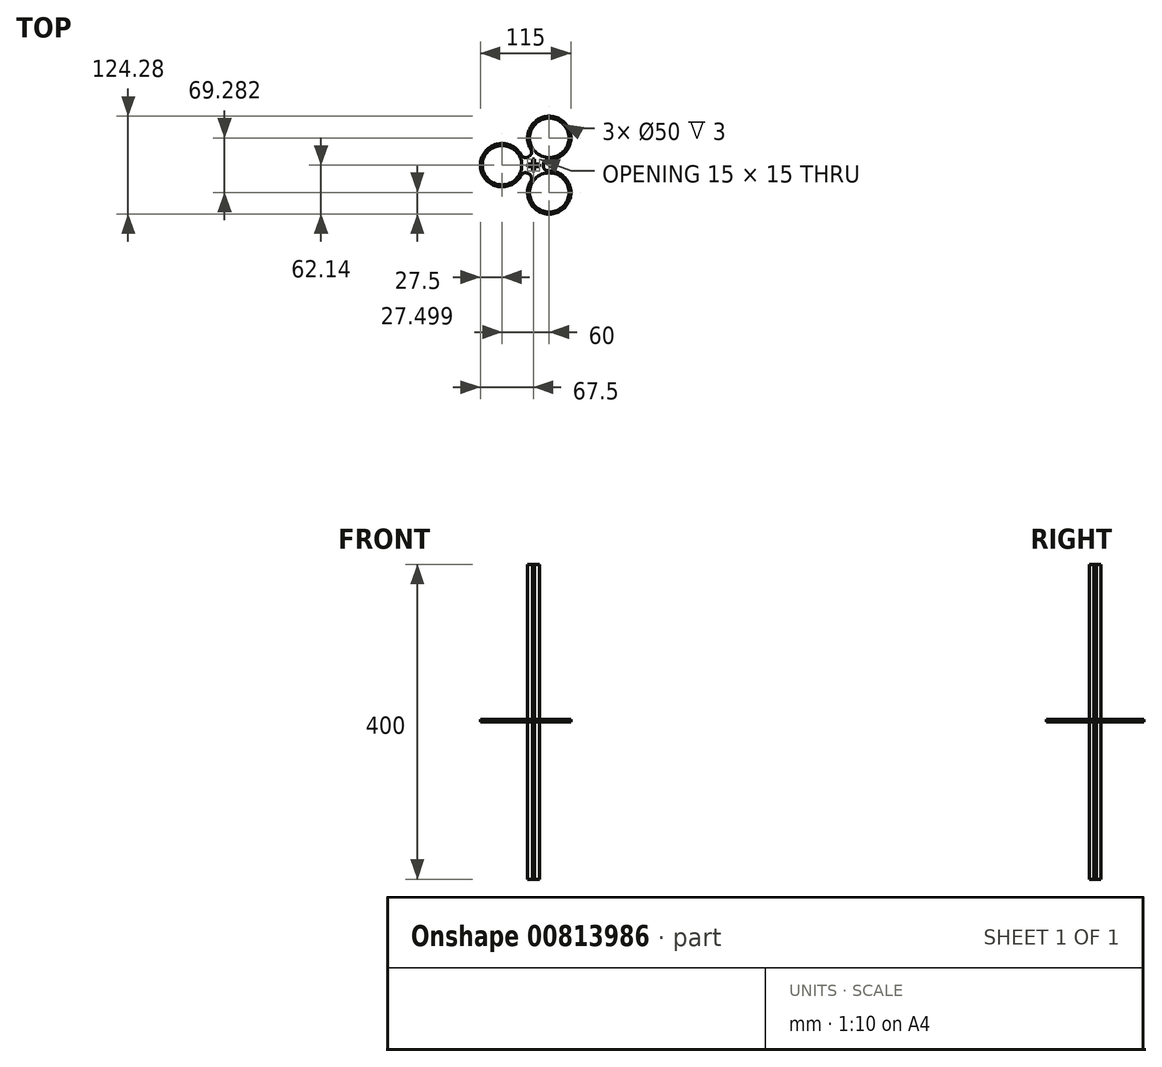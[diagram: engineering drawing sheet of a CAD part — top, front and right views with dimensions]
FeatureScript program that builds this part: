
annotation { "Feature Type Name" : "Feature", "Feature Type Description" : "" }
export const myFeature = defineFeature(function(context is Context, id is Id, definition is map)
    precondition{}
    {
        {
            assignVariable(context, id + "F0", {"variableType" : VariableType.LENGTH, "name" : "wt", "lengthValue" : 3 * mm});
        }
        {
            var Q0;
            Q0=qCreatedBy(makeId("Top.planeOp"),FACE);
            var sketch = newSketch(context, id + "F1", { "sketchPlane" : qUnion([Q0])});
            skCircle(sketch, "E0", {"center": v(0, 0) * mm, "radius": 12.5 * mm});
            skCircle(sketch, "E1", {"center": v(-40, 0) * mm, "radius": 27.5 * mm});
            skLineSegment(sketch, "E2", {"start": v(20, 34.64) * mm, "end": v(-40, 0) * mm, "construction": true});
            skPoint(sketch, "E3", {"position": v(-10, 17.32) * mm});
            skLineSegment(sketch, "E4", {"start": v(-10, 17.32) * mm, "end": v(0, 0) * mm, "construction": true});
            skLineSegment(sketch, "E5", {"start": v(20, 34.64) * mm, "end": v(20, -34.64) * mm, "construction": true});
            skLineSegment(sketch, "E6", {"start": v(-40, 0) * mm, "end": v(20, -34.64) * mm, "construction": true});
            skLineSegment(sketch, "E7", {"start": v(0, 0) * mm, "end": v(20, 0) * mm, "construction": true});
            skLineSegment(sketch, "E8", {"start": v(0, 0) * mm, "end": v(-10, -17.32) * mm, "construction": true});
            skLineSegment(sketch, "E9.bottom", {"start": v(-7.5, 1.5) * mm, "end": v(7.5, 1.5) * mm});
            skLineSegment(sketch, "E9.top", {"start": v(-7.5, -1.5) * mm, "end": v(7.5, -1.5) * mm});
            skLineSegment(sketch, "E9.left", {"start": v(-7.5, 1.5) * mm, "end": v(-7.5, -1.5) * mm});
            skLineSegment(sketch, "E9.right", {"start": v(7.5, 1.5) * mm, "end": v(7.5, -1.5) * mm});
            skLineSegment(sketch, "E10.bottom", {"start": v(-1.5, 7.5) * mm, "end": v(1.5, 7.5) * mm});
            skLineSegment(sketch, "E10.top", {"start": v(-1.5, -7.5) * mm, "end": v(1.5, -7.5) * mm});
            skLineSegment(sketch, "E10.left", {"start": v(-1.5, 7.5) * mm, "end": v(-1.5, -7.5) * mm});
            skLineSegment(sketch, "E10.right", {"start": v(1.5, 7.5) * mm, "end": v(1.5, -7.5) * mm});
            skCircle(sketch, "E11", {"center": v(-40, 0) * mm, "radius": 25 * mm});
            skCircle(sketch, "E12.1.0", {"center": v(20, -34.64) * mm, "radius": 27.5 * mm});
            skCircle(sketch, "E12.1.1", {"center": v(20, -34.64) * mm, "radius": 25 * mm});
            skCircle(sketch, "E12.2.0", {"center": v(20, 34.64) * mm, "radius": 27.5 * mm});
            skCircle(sketch, "E12.2.1", {"center": v(20, 34.64) * mm, "radius": 25 * mm});
            skFitSpline(sketch, "E13", {"points": [v(-16.18, 13.75) * mm, v(-6.25, 10.83) * mm, v(-3.82, 20.9) * mm], "startDerivative": vector(16.88, -30.59) * mm, "endDerivative": vector(-18.05, 29.91) * mm});
            skFitSpline(sketch, "E14", {"points": [v(20, 7.14) * mm, v(12.5, 0) * mm, v(20, -7.14) * mm], "startDerivative": vector(-34.93, 0.67) * mm, "endDerivative": vector(34.93, 0.67) * mm});
            skFitSpline(sketch, "E15", {"points": [v(-3.82, -20.9) * mm, v(-6.25, -10.83) * mm, v(-16.18, -13.75) * mm], "startDerivative": vector(18.05, 29.91) * mm, "endDerivative": vector(-16.88, -30.59) * mm});
            skLineSegment(sketch, "E16", {"start": v(20, 34.64) * mm, "end": v(14.18, 7.25) * mm, "construction": true});
            skLineSegment(sketch, "E17.MirrorCS", {"start": v(20, -34.64) * mm, "end": v(14.18, -7.25) * mm, "construction": true});
            skLineSegment(sketch, "E18", {"start": v(20, -34.64) * mm, "end": v(-0.8, -15.9) * mm, "construction": true});
            skLineSegment(sketch, "E19.MirrorCS", {"start": v(-40, 0) * mm, "end": v(-13.37, -8.65) * mm, "construction": true});
            skLineSegment(sketch, "E20.MirrorCS", {"start": v(-40, 0) * mm, "end": v(-13.37, 8.65) * mm, "construction": true});
            skLineSegment(sketch, "E21.MirrorCS", {"start": v(20, 34.64) * mm, "end": v(-0.8, 15.9) * mm, "construction": true});
            skSolve(sketch);
        }
        {
            var Q0;
            Q0=makeQuery(id+"F1.imprint","IMPRINT",FACE,{"disambiguationData":[TD([[makeQuery(id+"F1.imprint","IMPRINT",EDGE,{"derivedFrom":sQuery(id+"F1.wireOp",EDGE,"E11")}),-1.0]])]});
            var Q1;
            {var subQ0=sQuery(id+"F1.wireOp",EDGE,"E13");var subQ1=sQuery(id+"F1.wireOp",EDGE,"E0");var subQ2=makeQuery(id+"F1.imprint","INTERSECT",VERTEX,{"derivedFrom":[subQ1,subQ0]});Q1=makeQuery(id+"F1.imprint","IMPRINT",FACE,{"disambiguationData":[TD([[makeQuery(id+"F1.imprint","IMPRINT",EDGE,{"disambiguationData":[TD([[subQ2,-1.0]])],"derivedFrom":subQ1}),-1.0]])]});}
            var Q2;
            {var subQ0=sQuery(id+"F1.wireOp",EDGE,"E13");var subQ1=sQuery(id+"F1.wireOp",EDGE,"E0");var subQ2=makeQuery(id+"F1.imprint","INTERSECT",VERTEX,{"derivedFrom":[subQ1,subQ0]});Q2=makeQuery(id+"F1.imprint","IMPRINT",FACE,{"disambiguationData":[TD([[makeQuery(id+"F1.imprint","IMPRINT",EDGE,{"disambiguationData":[TD([[subQ2,1.0]])],"derivedFrom":subQ1}),-1.0]])]});}
            var Q3;
            Q3=makeQuery(id+"F1.imprint","IMPRINT",FACE,{"disambiguationData":[TD([[makeQuery(id+"F1.imprint","IMPRINT",EDGE,{"derivedFrom":sQuery(id+"F1.wireOp",EDGE,"E12.2.1")}),-1.0]])]});
            var Q4;
            {var subQ0=sQuery(id+"F1.wireOp",EDGE,"E14");var subQ1=sQuery(id+"F1.wireOp",EDGE,"E0");var subQ2=makeQuery(id+"F1.imprint","INTERSECT",VERTEX,{"derivedFrom":[subQ1,subQ0]});Q4=makeQuery(id+"F1.imprint","IMPRINT",FACE,{"disambiguationData":[TD([[makeQuery(id+"F1.imprint","IMPRINT",EDGE,{"disambiguationData":[TD([[subQ2,-1.0]])],"derivedFrom":subQ1}),-1.0]])]});}
            var Q5;
            {var subQ0=sQuery(id+"F1.wireOp",EDGE,"E9.left");Q5=makeQuery(id+"F1.imprint","IMPRINT",FACE,{"disambiguationData":[TD([[makeQuery(id+"F1.imprint","IMPRINT",EDGE,{"derivedFrom":subQ0}),-1.0]])]});}
            var Q6;
            {var subQ0=sQuery(id+"F1.wireOp",EDGE,"E15");var subQ1=sQuery(id+"F1.wireOp",EDGE,"E0");var subQ2=makeQuery(id+"F1.imprint","INTERSECT",VERTEX,{"derivedFrom":[subQ1,subQ0]});Q6=makeQuery(id+"F1.imprint","IMPRINT",FACE,{"disambiguationData":[TD([[makeQuery(id+"F1.imprint","IMPRINT",EDGE,{"disambiguationData":[TD([[subQ2,1.0]])],"derivedFrom":subQ1}),-1.0]])]});}
            var Q7;
            {var subQ0=sQuery(id+"F1.wireOp",EDGE,"E15");var subQ1=sQuery(id+"F1.wireOp",EDGE,"E0");var subQ2=makeQuery(id+"F1.imprint","INTERSECT",VERTEX,{"derivedFrom":[subQ1,subQ0]});Q7=makeQuery(id+"F1.imprint","IMPRINT",FACE,{"disambiguationData":[TD([[makeQuery(id+"F1.imprint","IMPRINT",EDGE,{"disambiguationData":[TD([[subQ2,-1.0]])],"derivedFrom":subQ1}),-1.0]])]});}
            var Q8;
            {var subQ0=sQuery(id+"F1.wireOp",EDGE,"E14");var subQ1=sQuery(id+"F1.wireOp",EDGE,"E0");var subQ2=makeQuery(id+"F1.imprint","INTERSECT",VERTEX,{"derivedFrom":[subQ1,subQ0]});Q8=makeQuery(id+"F1.imprint","IMPRINT",FACE,{"disambiguationData":[TD([[makeQuery(id+"F1.imprint","IMPRINT",EDGE,{"disambiguationData":[TD([[subQ2,1.0]])],"derivedFrom":subQ1}),-1.0]])]});}
            var Q9;
            Q9=makeQuery(id+"F1.imprint","IMPRINT",FACE,{"disambiguationData":[TD([[makeQuery(id+"F1.imprint","IMPRINT",EDGE,{"derivedFrom":sQuery(id+"F1.wireOp",EDGE,"E12.1.1")}),-1.0]])]});
            extrude(context, id + "F2", {"entities" : qUnion([Q0, Q1, Q2, Q3, Q4, Q5, Q6, Q7, Q8, Q9]), "depth" : getVariable(context, 'wt'), "offsetDistance" : 25 * mm});
        }
        {
            var Q0;
            {var subQ0=sQuery(id+"F1.wireOp",EDGE,"E9.left");Q0=makeQuery(id+"F1.imprint","IMPRINT",FACE,{"disambiguationData":[TD([[makeQuery(id+"F1.imprint","IMPRINT",EDGE,{"derivedFrom":subQ0}),1.0]])]});}
            var Q1;
            {var subQ0=sQuery(id+"F1.wireOp",EDGE,"E10.left");var subQ1=sQuery(id+"F1.wireOp",EDGE,"E9.bottom");var subQ2=makeQuery(id+"F1.imprint","INTERSECT",VERTEX,{"derivedFrom":[subQ1,subQ0]});Q1=makeQuery(id+"F1.imprint","IMPRINT",FACE,{"disambiguationData":[TD([[makeQuery(id+"F1.imprint","IMPRINT",EDGE,{"disambiguationData":[TD([[subQ2,-1.0]])],"derivedFrom":subQ1}),-1.0]])]});}
            var Q2;
            {var subQ0=sQuery(id+"F1.wireOp",EDGE,"E9.right");Q2=makeQuery(id+"F1.imprint","IMPRINT",FACE,{"disambiguationData":[TD([[makeQuery(id+"F1.imprint","IMPRINT",EDGE,{"derivedFrom":subQ0}),-1.0]])]});}
            extrude(context, id + "F3", {"entities" : qUnion([Q0, Q1, Q2]), "depth" : 200 * mm, "offsetDistance" : 25 * mm, "hasSecondDirection" : true, "secondDirectionOppositeDirection" : true, "secondDirectionDepth" : 200 * mm});
        }
        {
            var Q0;
            {var subQ5=sQuery(id+"F1.wireOp",EDGE,"E10.top");Q0=makeQuery(id+"F1.imprint","IMPRINT",FACE,{"disambiguationData":[TD([[makeQuery(id+"F1.imprint","IMPRINT",EDGE,{"derivedFrom":subQ5}),1.0]])]});}
            var Q1;
            {var subQ0=sQuery(id+"F1.wireOp",EDGE,"E10.left");var subQ1=sQuery(id+"F1.wireOp",EDGE,"E9.bottom");var subQ2=makeQuery(id+"F1.imprint","INTERSECT",VERTEX,{"derivedFrom":[subQ1,subQ0]});Q1=makeQuery(id+"F1.imprint","IMPRINT",FACE,{"disambiguationData":[TD([[makeQuery(id+"F1.imprint","IMPRINT",EDGE,{"disambiguationData":[TD([[subQ2,-1.0]])],"derivedFrom":subQ1}),-1.0]])]});}
            var Q2;
            {var subQ5=sQuery(id+"F1.wireOp",EDGE,"E10.bottom");Q2=makeQuery(id+"F1.imprint","IMPRINT",FACE,{"disambiguationData":[TD([[makeQuery(id+"F1.imprint","IMPRINT",EDGE,{"derivedFrom":subQ5}),-1.0]])]});}
            extrude(context, id + "F4", {"entities" : qUnion([Q0, Q1, Q2]), "depth" : 200 * mm, "offsetDistance" : 25 * mm, "hasSecondDirection" : true, "secondDirectionOppositeDirection" : true, "secondDirectionDepth" : 200 * mm});
        }
    });
